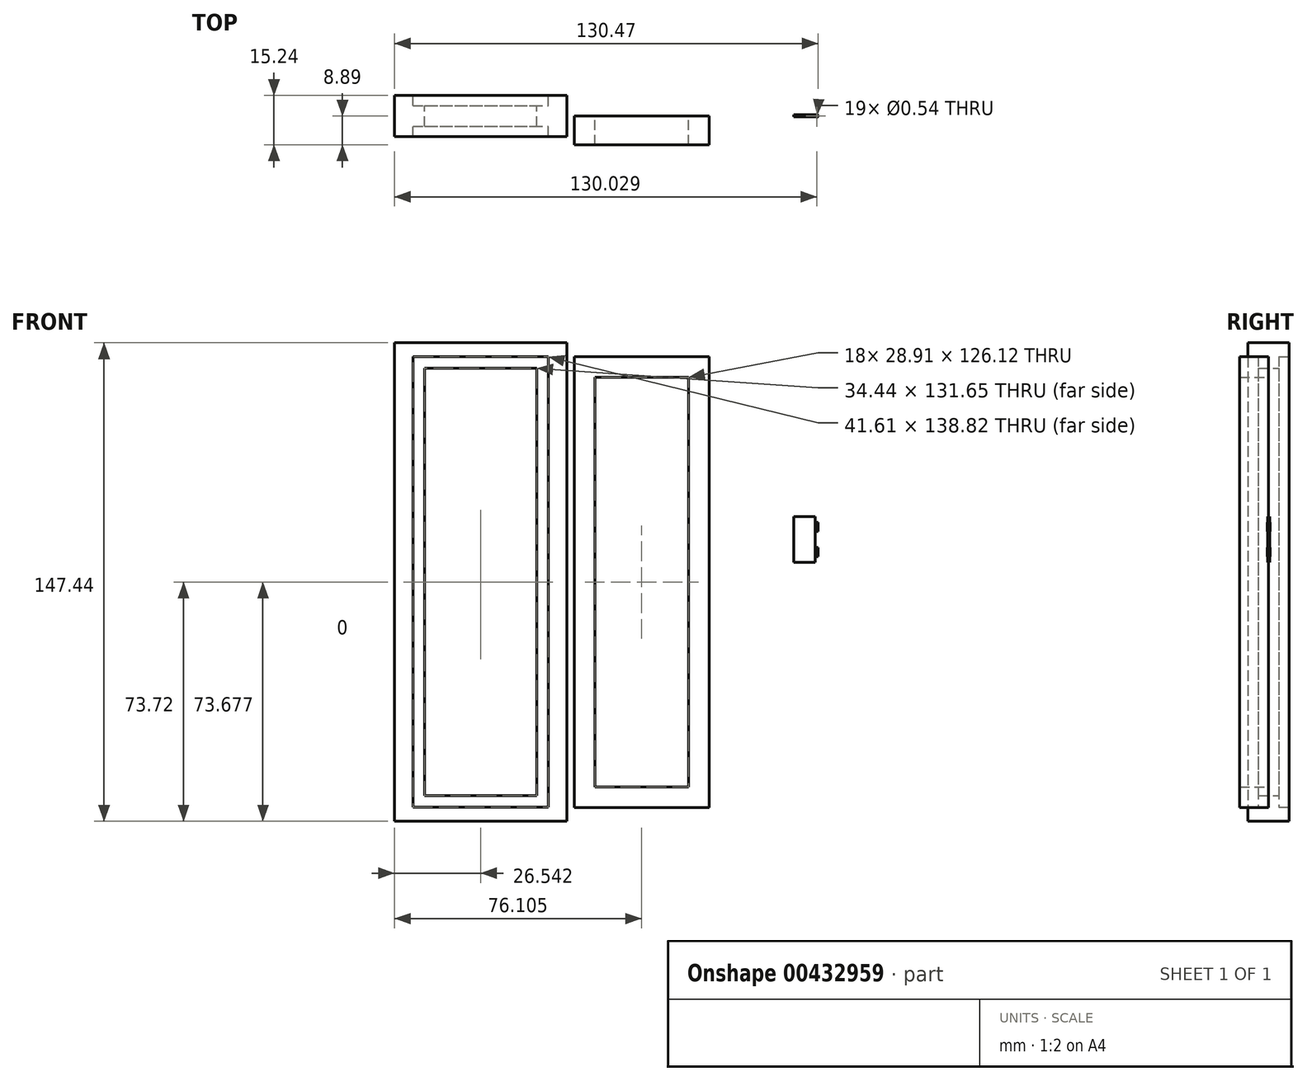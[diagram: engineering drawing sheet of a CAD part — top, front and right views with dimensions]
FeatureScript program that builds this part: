
annotation { "Feature Type Name" : "Feature", "Feature Type Description" : "" }
export const myFeature = defineFeature(function(context is Context, id is Id, definition is map)
    precondition{}
    {
        {
            var Q0;
            Q0=qCreatedBy(makeId("Front.planeOp"),FACE);
            var sketch = newSketch(context, id + "F0", { "sketchPlane" : qUnion([Q0])});
            skLineSegment(sketch, "E0.bottom", {"start": v(-94.36, 73.72) * mm, "end": v(-41.27, 73.72) * mm});
            skLineSegment(sketch, "E0.top", {"start": v(-94.36, -73.72) * mm, "end": v(-41.27, -73.72) * mm});
            skLineSegment(sketch, "E0.left", {"start": v(-94.36, 73.72) * mm, "end": v(-94.36, -73.72) * mm});
            skLineSegment(sketch, "E0.right", {"start": v(-41.27, 73.72) * mm, "end": v(-41.27, -73.72) * mm});
            skPoint(sketch, "E0.middle", {"position": v(0, 0) * mm});
            skLineSegment(sketch, "E1.bottom", {"start": v(-88.62, 69.41) * mm, "end": v(-47.01, 69.41) * mm});
            skLineSegment(sketch, "E1.top", {"start": v(-88.62, -69.41) * mm, "end": v(-47.01, -69.41) * mm});
            skLineSegment(sketch, "E1.left", {"start": v(-88.62, 69.41) * mm, "end": v(-88.62, -69.41) * mm});
            skLineSegment(sketch, "E1.right", {"start": v(-47.01, 69.41) * mm, "end": v(-47.01, -69.41) * mm});
            skLineSegment(sketch, "E2.bottom", {"start": v(-85.04, 65.82) * mm, "end": v(-50.6, 65.82) * mm});
            skLineSegment(sketch, "E2.top", {"start": v(-85.04, -65.82) * mm, "end": v(-50.6, -65.82) * mm});
            skLineSegment(sketch, "E2.left", {"start": v(-85.04, 65.82) * mm, "end": v(-85.04, -65.82) * mm});
            skLineSegment(sketch, "E2.right", {"start": v(-50.6, 65.82) * mm, "end": v(-50.6, -65.82) * mm});
            skSolve(sketch);
        }
        {
            var Q0;
            Q0=makeQuery(id+"F0.imprint","IMPRINT",FACE,{"disambiguationData":[TD([[makeQuery(id+"F0.imprint","IMPRINT",EDGE,{"derivedFrom":sQuery(id+"F0.wireOp",EDGE,"E1.bottom")}),-1.0]])]});
            extrude(context, id + "F1", {"entities" : qUnion([Q0]), "endBound" : BoundingType.SYMMETRIC, "depth" : 6.35 * mm});
        }
        {
            var Q0;
            Q0=makeQuery(id+"F0.imprint","IMPRINT",FACE,{"disambiguationData":[TD([[makeQuery(id+"F0.imprint","IMPRINT",EDGE,{"derivedFrom":sQuery(id+"F0.wireOp",EDGE,"E0.bottom")}),-1.0]])]});
            extrude(context, id + "F2", {"entities" : qUnion([Q0]), "operationType" : NewBodyOperationType.ADD, "endBound" : BoundingType.SYMMETRIC, "depth" : 12.7 * mm});
        }
        {
            var Q0;
            Q0=qCreatedBy(makeId("Front.planeOp"),FACE);
            var sketch = newSketch(context, id + "F3", { "sketchPlane" : qUnion([Q0])});
            skPoint(sketch, "E3.middle", {"position": v(0, 0) * mm});
            skLineSegment(sketch, "E4.bottom", {"start": v(-39.06, 69.37) * mm, "end": v(2.55, 69.37) * mm});
            skLineSegment(sketch, "E4.top", {"start": v(-39.06, -69.45) * mm, "end": v(2.55, -69.45) * mm});
            skLineSegment(sketch, "E4.left", {"start": v(-39.06, 69.37) * mm, "end": v(-39.06, -69.45) * mm});
            skLineSegment(sketch, "E4.right", {"start": v(2.55, 69.37) * mm, "end": v(2.55, -69.45) * mm});
            skLineSegment(sketch, "E5.0", {"start": v(-32.71, 63.02) * mm, "end": v(-3.8, 63.02) * mm});
            skLineSegment(sketch, "E5.1", {"start": v(-32.71, 63.02) * mm, "end": v(-32.71, -63.1) * mm});
            skLineSegment(sketch, "E5.2", {"start": v(-32.71, -63.1) * mm, "end": v(-3.8, -63.1) * mm});
            skLineSegment(sketch, "E5.3", {"start": v(-3.8, 63.02) * mm, "end": v(-3.8, -63.1) * mm});
            skSolve(sketch);
        }
        {
            var Q0;
            Q0=makeQuery(id+"F3.imprint","IMPRINT",FACE,{"disambiguationData":[TD([[makeQuery(id+"F3.imprint","IMPRINT",EDGE,{"derivedFrom":sQuery(id+"F3.wireOp",EDGE,"E4.bottom")}),-1.0]])]});
            extrude(context, id + "F4", {"entities" : qUnion([Q0]), "depth" : 8.9 * mm});
        }
        {
            var Q0;
            Q0=qCreatedBy(makeId("Front.planeOp"),FACE);
            var sketch = newSketch(context, id + "F5", { "sketchPlane" : qUnion([Q0])});
            skLineSegment(sketch, "E6.bottom", {"start": v(28.51, 20.2) * mm, "end": v(35.23, 20.2) * mm});
            skLineSegment(sketch, "E6.top", {"start": v(28.51, 6.08) * mm, "end": v(35.23, 6.08) * mm});
            skLineSegment(sketch, "E6.left", {"start": v(28.51, 20.2) * mm, "end": v(28.51, 6.08) * mm});
            skLineSegment(sketch, "E6.right", {"start": v(35.23, 20.2) * mm, "end": v(35.23, 6.08) * mm});
            skPoint(sketch, "E6.middle", {"position": v(31.87, 13.14) * mm});
            skLineSegment(sketch, "E7.bottom", {"start": v(35.23, 18.36) * mm, "end": v(36.1, 18.36) * mm});
            skLineSegment(sketch, "E7.top", {"start": v(35.23, 15.64) * mm, "end": v(36.1, 15.64) * mm});
            skLineSegment(sketch, "E7.left", {"start": v(35.23, 18.36) * mm, "end": v(35.23, 15.64) * mm});
            skLineSegment(sketch, "E7.right", {"start": v(36.1, 18.36) * mm, "end": v(36.1, 15.64) * mm});
            skPoint(sketch, "E7.middle", {"position": v(35.67, 17) * mm});
            skLineSegment(sketch, "E8", {"start": v(35.67, 18.36) * mm, "end": v(35.67, 15.64) * mm});
            skLineSegment(sketch, "E9.bottom", {"start": v(35.4, 18.36) * mm, "end": v(35.94, 18.36) * mm});
            skLineSegment(sketch, "E9.top", {"start": v(35.4, 15.64) * mm, "end": v(35.94, 15.64) * mm});
            skLineSegment(sketch, "E9.left", {"start": v(35.4, 18.36) * mm, "end": v(35.4, 15.64) * mm});
            skLineSegment(sketch, "E9.right", {"start": v(35.94, 18.36) * mm, "end": v(35.94, 15.64) * mm});
            skLineSegment(sketch, "E10.bottom", {"start": v(35.23, 10.58) * mm, "end": v(36.1, 10.58) * mm});
            skLineSegment(sketch, "E10.top", {"start": v(35.23, 7.85) * mm, "end": v(36.1, 7.85) * mm});
            skLineSegment(sketch, "E10.left", {"start": v(35.23, 10.58) * mm, "end": v(35.23, 7.85) * mm});
            skLineSegment(sketch, "E10.right", {"start": v(36.1, 10.58) * mm, "end": v(36.1, 7.85) * mm});
            skPoint(sketch, "E10.middle", {"position": v(35.67, 9.22) * mm});
            skLineSegment(sketch, "E11", {"start": v(35.67, 10.58) * mm, "end": v(35.67, 7.85) * mm});
            skLineSegment(sketch, "E12.bottom", {"start": v(35.4, 10.58) * mm, "end": v(35.94, 10.58) * mm});
            skLineSegment(sketch, "E12.top", {"start": v(35.4, 7.85) * mm, "end": v(35.94, 7.85) * mm});
            skLineSegment(sketch, "E12.left", {"start": v(35.4, 10.58) * mm, "end": v(35.4, 7.85) * mm});
            skLineSegment(sketch, "E12.right", {"start": v(35.94, 10.58) * mm, "end": v(35.94, 7.85) * mm});
            skSolve(sketch);
        }
        {
            var Q0;
            {var subQ0=sQuery(id+"F5.wireOp",EDGE,"E7.right");Q0=makeQuery(id+"F5.imprint","IMPRINT",FACE,{"disambiguationData":[TD([[makeQuery(id+"F5.imprint","IMPRINT",EDGE,{"derivedFrom":subQ0}),-1.0]])]});}
            var Q1;
            Q1 = qSketchRegion(id + "FxaQCcS6UFXWdTR", true);
            var Q2;
            Q2=sQuery(id+"F5.wireOp",EDGE,"E8");
            revolve(context, id + "F6", {"entities" : qUnion([Q0, Q1]), "axis" : qUnion([Q2]), "revolveType" : RevolveType.FULL});
        }
        {
            var Q0;
            {var subQ1=sQuery(id+"F5.wireOp",EDGE,"E6.bottom");Q0=makeQuery(id+"F5.imprint","IMPRINT",FACE,{"disambiguationData":[TD([[makeQuery(id+"F5.imprint","IMPRINT",EDGE,{"derivedFrom":subQ1}),-1.0]])]});}
            extrude(context, id + "F7", {"entities" : qUnion([Q0]), "endBound" : BoundingType.SYMMETRIC, "depth" : 0.64 * mm});
        }
        {
            var Q0;
            {var subQ0=sQuery(id+"F5.wireOp",EDGE,"E10.right");Q0=makeQuery(id+"F5.imprint","IMPRINT",FACE,{"disambiguationData":[TD([[makeQuery(id+"F5.imprint","IMPRINT",EDGE,{"derivedFrom":subQ0}),-1.0]])]});}
            var Q1;
            Q1=sQuery(id+"F5.wireOp",EDGE,"E11");
            revolve(context, id + "F8", {"operationType" : NewBodyOperationType.ADD, "entities" : qUnion([Q0]), "axis" : qUnion([Q1]), "revolveType" : RevolveType.FULL});
        }
    });
